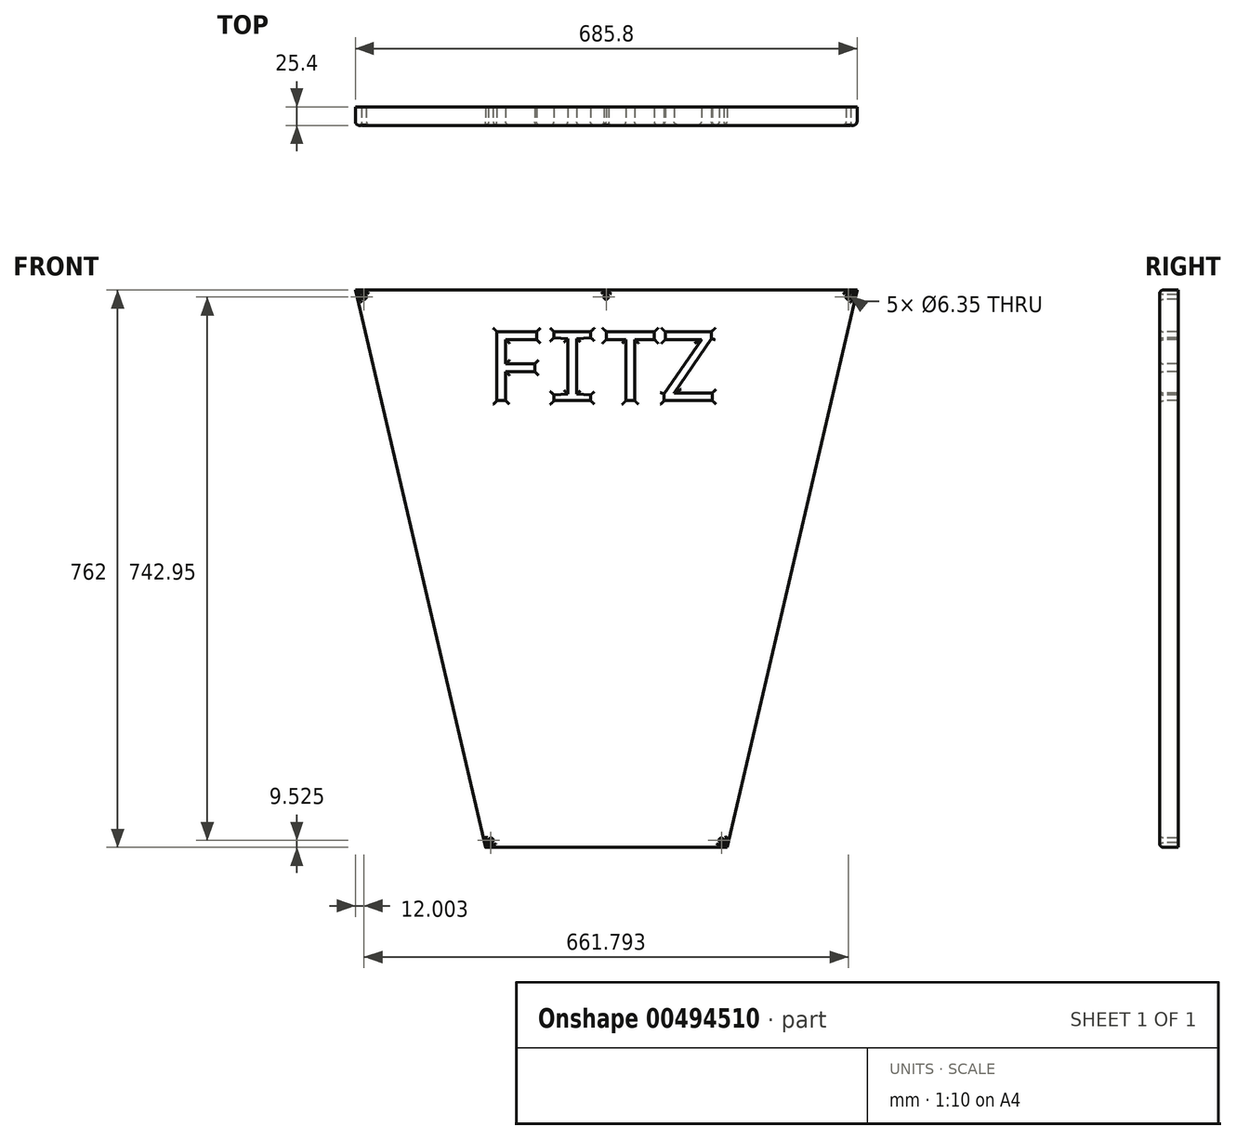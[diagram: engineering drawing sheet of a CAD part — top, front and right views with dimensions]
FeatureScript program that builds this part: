
annotation { "Feature Type Name" : "Feature", "Feature Type Description" : "" }
export const myFeature = defineFeature(function(context is Context, id is Id, definition is map)
    precondition{}
    {
        {
            var Q0;
            Q0=qCreatedBy(makeId("Front.planeOp"),FACE);
            var sketch = newSketch(context, id + "F0", { "sketchPlane" : qUnion([Q0])});
            skLineSegment(sketch, "E0", {"start": v(0, 0) * mm, "end": v(685.8, 0) * mm});
            skLineSegment(sketch, "E1", {"start": v(0, 0) * mm, "end": v(342.9, 0) * mm, "construction": true});
            skLineSegment(sketch, "E2", {"start": v(342.9, 0) * mm, "end": v(342.9, -762) * mm, "construction": true});
            skLineSegment(sketch, "E3", {"start": v(342.9, -762) * mm, "end": v(508, -762) * mm});
            skLineSegment(sketch, "E4", {"start": v(342.9, -762) * mm, "end": v(177.8, -762) * mm});
            skLineSegment(sketch, "E5", {"start": v(508, -762) * mm, "end": v(685.8, 0) * mm});
            skLineSegment(sketch, "E6", {"start": v(177.8, -762) * mm, "end": v(0, 0) * mm});
            skText(sketch, "E7", { "text": "FITZ", "fontName": "DroidSansMono.ttf"});
            skCircle(sketch, "E8", {"center": v(12, -9.53) * mm, "radius": 3.18 * mm});
            skCircle(sketch, "E9", {"center": v(673.8, -9.53) * mm, "radius": 3.18 * mm});
            skCircle(sketch, "E10", {"center": v(342.9, -9.53) * mm, "radius": 3.18 * mm});
            skCircle(sketch, "E11", {"center": v(185.36, -752.48) * mm, "radius": 3.18 * mm});
            skCircle(sketch, "E12", {"center": v(500.44, -752.48) * mm, "radius": 3.18 * mm});
            const initialGuessF0  = {"E7": [0.17787, -0.15135, 1, 0, 0.09508]};
            skSetInitialGuess(sketch, initialGuessF0);
            skSolve(sketch);
        }
        {
            var Q0;
            Q0 = qSketchRegion(id + "F0", true);
            extrude(context, id + "F1", {"entities" : qUnion([Q0]), "oppositeDirection" : true, "depth" : 25.4 * mm});
        }
        {
            var Q0;
            Q0=makeQuery(id+"F1.opExtrude","CAP_FACE",FACE,{"disambiguationData":[OSD([sQuery(id+"F0.wireOp",EDGE,"E0"),sQuery(id+"F0.wireOp",EDGE,"E3"),sQuery(id+"F0.wireOp",EDGE,"E4"),sQuery(id+"F0.wireOp",EDGE,"E5"),sQuery(id+"F0.wireOp",EDGE,"E6"),sQuery(id+"F0.wireOp",EDGE,"E7.sketch_text.stroke-0"),sQuery(id+"F0.wireOp",EDGE,"E7.sketch_text.stroke-1"),sQuery(id+"F0.wireOp",EDGE,"E7.sketch_text.stroke-2"),sQuery(id+"F0.wireOp",EDGE,"E7.sketch_text.stroke-3"),sQuery(id+"F0.wireOp",EDGE,"E7.sketch_text.stroke-4"),sQuery(id+"F0.wireOp",EDGE,"E7.sketch_text.stroke-5"),sQuery(id+"F0.wireOp",EDGE,"E7.sketch_text.stroke-6"),sQuery(id+"F0.wireOp",EDGE,"E7.sketch_text.stroke-7"),sQuery(id+"F0.wireOp",EDGE,"E7.sketch_text.stroke-8"),sQuery(id+"F0.wireOp",EDGE,"E7.sketch_text.stroke-9"),sQuery(id+"F0.wireOp",EDGE,"E7.sketch_text.stroke-10"),sQuery(id+"F0.wireOp",EDGE,"E7.sketch_text.stroke-11"),sQuery(id+"F0.wireOp",EDGE,"E7.sketch_text.stroke-12"),sQuery(id+"F0.wireOp",EDGE,"E7.sketch_text.stroke-13"),sQuery(id+"F0.wireOp",EDGE,"E7.sketch_text.stroke-14"),sQuery(id+"F0.wireOp",EDGE,"E7.sketch_text.stroke-15"),sQuery(id+"F0.wireOp",EDGE,"E7.sketch_text.stroke-16"),sQuery(id+"F0.wireOp",EDGE,"E7.sketch_text.stroke-17"),sQuery(id+"F0.wireOp",EDGE,"E7.sketch_text.stroke-18"),sQuery(id+"F0.wireOp",EDGE,"E7.sketch_text.stroke-19"),sQuery(id+"F0.wireOp",EDGE,"E7.sketch_text.stroke-20"),sQuery(id+"F0.wireOp",EDGE,"E7.sketch_text.stroke-21"),sQuery(id+"F0.wireOp",EDGE,"E7.sketch_text.stroke-22"),sQuery(id+"F0.wireOp",EDGE,"E7.sketch_text.stroke-23"),sQuery(id+"F0.wireOp",EDGE,"E7.sketch_text.stroke-24"),sQuery(id+"F0.wireOp",EDGE,"E7.sketch_text.stroke-25"),sQuery(id+"F0.wireOp",EDGE,"E7.sketch_text.stroke-26"),sQuery(id+"F0.wireOp",EDGE,"E7.sketch_text.stroke-27"),sQuery(id+"F0.wireOp",EDGE,"E7.sketch_text.stroke-28"),sQuery(id+"F0.wireOp",EDGE,"E7.sketch_text.stroke-29"),sQuery(id+"F0.wireOp",EDGE,"E7.sketch_text.stroke-30"),sQuery(id+"F0.wireOp",EDGE,"E7.sketch_text.stroke-31"),sQuery(id+"F0.wireOp",EDGE,"E7.sketch_text.stroke-32"),sQuery(id+"F0.wireOp",EDGE,"E7.sketch_text.stroke-33"),sQuery(id+"F0.wireOp",EDGE,"E7.sketch_text.stroke-34"),sQuery(id+"F0.wireOp",EDGE,"E7.sketch_text.stroke-35"),sQuery(id+"F0.wireOp",EDGE,"E7.sketch_text.stroke-36"),sQuery(id+"F0.wireOp",EDGE,"E7.sketch_text.stroke-37"),sQuery(id+"F0.wireOp",EDGE,"E7.sketch_text.stroke-38"),sQuery(id+"F0.wireOp",EDGE,"E7.sketch_text.stroke-39")])],"isStart":true});
            fillet(context, id + "F2", {"entities" : qUnion([Q0]), "radius" : 5.08 * mm, "tangentPropagation" : true, "allowEdgeOverflow" : false});
        }
    });
